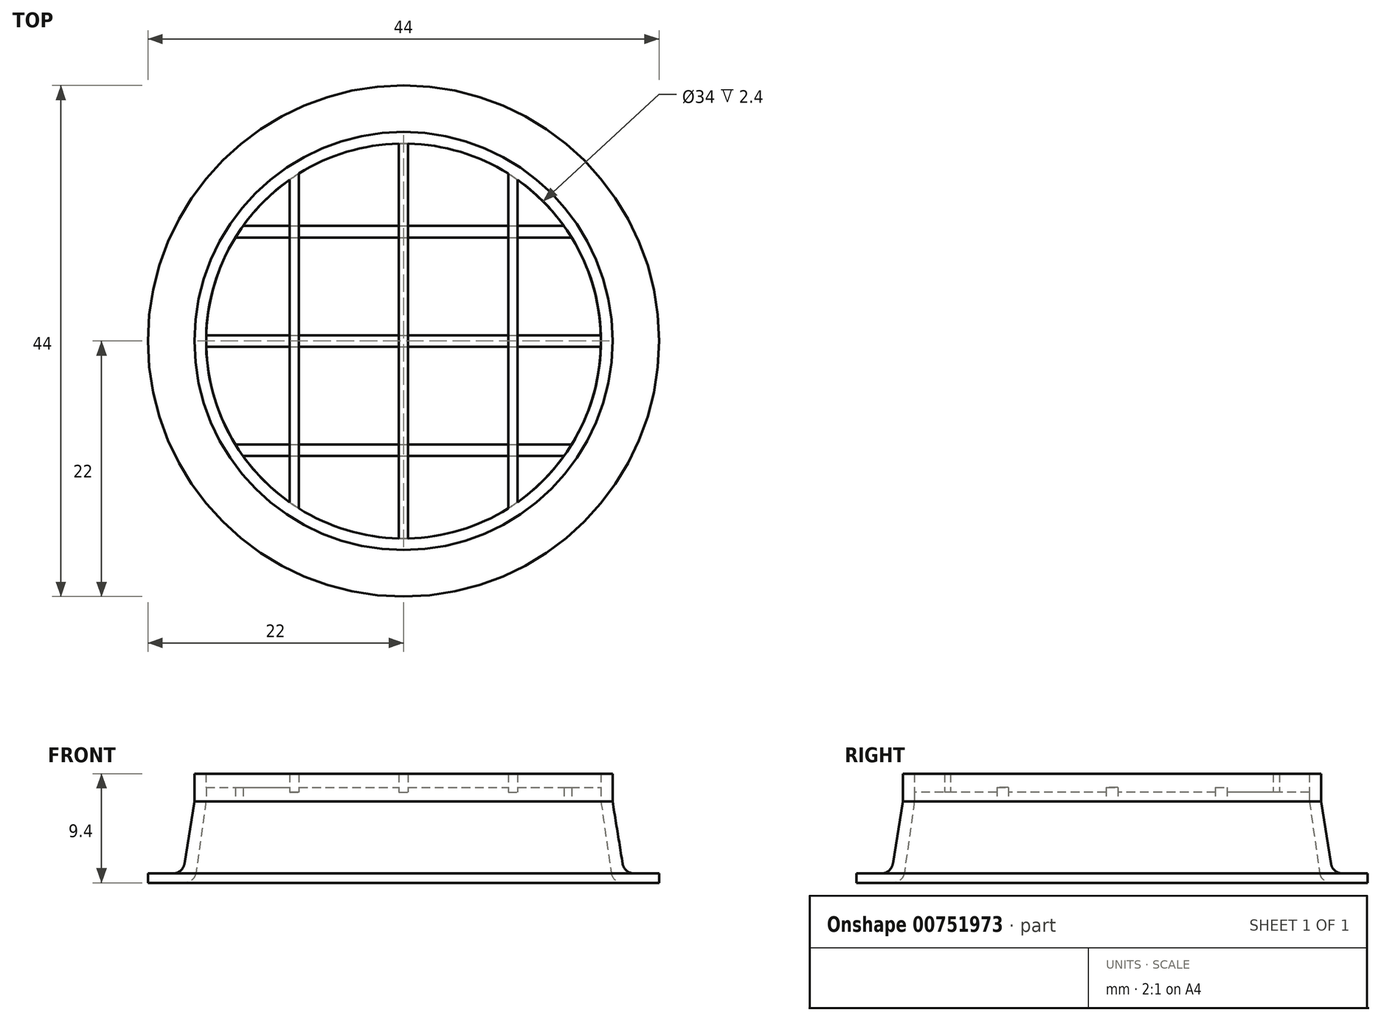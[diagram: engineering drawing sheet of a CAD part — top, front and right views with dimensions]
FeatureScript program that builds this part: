
annotation { "Feature Type Name" : "Feature", "Feature Type Description" : "" }
export const myFeature = defineFeature(function(context is Context, id is Id, definition is map)
    precondition{}
    {
        {
            var Q0;
            Q0=qCreatedBy(makeId("Front.planeOp"),FACE);
            var sketch = newSketch(context, id + "F0", { "sketchPlane" : qUnion([Q0])});
            skLineSegment(sketch, "E0", {"start": v(0, 16.66) * mm, "end": v(0, -15.75) * mm, "construction": true});
            skLineSegment(sketch, "E1", {"start": v(8.08, 0) * mm, "end": v(-29.3, 0) * mm, "construction": true});
            skLineSegment(sketch, "E2", {"start": v(1.58, 0) * mm, "end": v(-1.66, 0) * mm, "construction": true});
            skLineSegment(sketch, "E3", {"start": v(-1, 1.45) * mm, "end": v(-1, -7.95) * mm, "construction": true});
            skLineSegment(sketch, "E4", {"start": v(-5, -6.2) * mm, "end": v(-5, -8.06) * mm, "construction": true});
            skLineSegment(sketch, "E5", {"start": v(-5, -7) * mm, "end": v(-1.87, -7) * mm});
            skLineSegment(sketch, "E6", {"start": v(-0.88, -6.14) * mm, "end": v(0, 0) * mm});
            skLineSegment(sketch, "E7", {"start": v(0, 0) * mm, "end": v(-1, 0) * mm});
            skLineSegment(sketch, "E8", {"start": v(-1, 0) * mm, "end": v(-1.86, -5.36) * mm});
            skLineSegment(sketch, "E9", {"start": v(-2.85, -6.2) * mm, "end": v(-5, -6.2) * mm});
            skLineSegment(sketch, "E10", {"start": v(-5, -6.2) * mm, "end": v(-5, -7) * mm});
            skPoint(sketch, "E11.visualSharp", {"position": v(-2, -6.2) * mm});
            skArc(sketch, "E11.filletArc", {"start": v(-2.85, -6.2) * mm, "mid": v(-2.2, -5.96) * mm, "end": v(-1.86, -5.36) * mm});
            skPoint(sketch, "E12.visualSharp", {"position": v(-1, -7) * mm});
            skArc(sketch, "E12.filletArc", {"start": v(-1.87, -7) * mm, "mid": v(-1.21, -6.76) * mm, "end": v(-0.88, -6.14) * mm});
            skLineSegment(sketch, "E13", {"start": v(17, 0.36) * mm, "end": v(17, -7.36) * mm, "construction": true});
            skSolve(sketch);
        }
        {
            var Q0;
            Q0=qSketchRegion(id+"F0",true);
            var Q1;
            Q1=sQuery(id+"F0.wireOp",EDGE,"E13");
            revolve(context, id + "F1", {"surfaceOperationType" : NewSurfaceOperationType.NEW, "entities" : qUnion([Q0]), "axis" : qUnion([Q1]), "revolveType" : RevolveType.FULL});
        }
        {
            var Q0;
            Q0=makeQuery(id+"F1.opRevolve","SWEPT_FACE",FACE,{"disambiguationData":[OSD([sQuery(id+"F0.wireOp",EDGE,"E7")])]});
            var sketch = newSketch(context, id + "F2", { "sketchPlane" : qUnion([Q0])});
            skLineSegment(sketch, "E14", {"start": v(0, 0) * mm, "end": v(34, 0) * mm, "construction": true});
            skCircle(sketch, "E15.0", {"center": v(17, 0) * mm, "radius": 18 * mm});
            skLineSegment(sketch, "E16", {"start": v(-1, 0.5) * mm, "end": v(35, 0.5) * mm});
            skLineSegment(sketch, "E17.MirrorCS", {"start": v(-1, -0.5) * mm, "end": v(35, -0.5) * mm});
            skLineSegment(sketch, "E18", {"start": v(1.36, 8.91) * mm, "end": v(32.64, 8.91) * mm});
            skLineSegment(sketch, "E19", {"start": v(1.97, 9.91) * mm, "end": v(32.03, 9.91) * mm});
            skLineSegment(sketch, "E20.MirrorCS", {"start": v(1.36, -8.91) * mm, "end": v(32.64, -8.91) * mm});
            skLineSegment(sketch, "E21.MirrorCS", {"start": v(1.97, -9.91) * mm, "end": v(32.03, -9.91) * mm});
            skSolve(sketch);
        }
        {
            var Q0;
            {var subQ0=sQuery(id+"F2.wireOp",EDGE,"E18");var subQ1=makeQuery(id+"F1.opRevolve","SWEPT_EDGE",EDGE,{"disambiguationData":[OSD([sQuery(id+"F0.wireOp",EDGE,"E6"),sQuery(id+"F0.wireOp",EDGE,"E7")])]});var subQ2=makeQuery(id+"F2.imprint","INTERSECT",VERTEX,{"disambiguationData":[OD(0.0)],"derivedFrom":[subQ1,subQ0]});Q0=makeQuery(id+"F2.imprint","IMPRINT",FACE,{"disambiguationData":[TD([[makeQuery(id+"F2.imprint","IMPRINT",EDGE,{"disambiguationData":[TD([[subQ2,-1.0]])],"derivedFrom":subQ0}),1.0]])]});}
            var Q1;
            {var subQ0=sQuery(id+"F2.wireOp",EDGE,"E16");var subQ1=makeQuery(id+"F1.opRevolve","SWEPT_EDGE",EDGE,{"disambiguationData":[OSD([sQuery(id+"F0.wireOp",EDGE,"E6"),sQuery(id+"F0.wireOp",EDGE,"E7")])]});var subQ2=makeQuery(id+"F2.imprint","INTERSECT",VERTEX,{"disambiguationData":[OD(0.0)],"derivedFrom":[subQ1,subQ0]});Q1=makeQuery(id+"F2.imprint","IMPRINT",FACE,{"disambiguationData":[TD([[makeQuery(id+"F2.imprint","IMPRINT",EDGE,{"disambiguationData":[TD([[subQ2,-1.0]])],"derivedFrom":subQ0}),-1.0]])]});}
            var Q2;
            {var subQ0=sQuery(id+"F2.wireOp",EDGE,"E20.MirrorCS");var subQ1=makeQuery(id+"F1.opRevolve","SWEPT_EDGE",EDGE,{"disambiguationData":[OSD([sQuery(id+"F0.wireOp",EDGE,"E6"),sQuery(id+"F0.wireOp",EDGE,"E7")])]});var subQ2=makeQuery(id+"F2.imprint","INTERSECT",VERTEX,{"disambiguationData":[OD(0.0)],"derivedFrom":[subQ1,subQ0]});Q2=makeQuery(id+"F2.imprint","IMPRINT",FACE,{"disambiguationData":[TD([[makeQuery(id+"F2.imprint","IMPRINT",EDGE,{"disambiguationData":[TD([[subQ2,-1.0]])],"derivedFrom":subQ0}),-1.0]])]});}
            extrude(context, id + "F3", {"entities" : qUnion([Q0, Q1, Q2]), "depth" : 1.2 * mm, "offsetDistance" : 25 * mm});
        }
        {
            var Q0;
            Q0=makeQuery(id+"F1.opRevolve","SWEPT_FACE",FACE,{"disambiguationData":[OSD([sQuery(id+"F0.wireOp",EDGE,"E7")])]});
            var sketch = newSketch(context, id + "F4", { "sketchPlane" : qUnion([Q0])});
            skCircle(sketch, "E22.0", {"center": v(17, 0) * mm, "radius": 17 * mm});
            skCircle(sketch, "E23.0", {"center": v(17, 0) * mm, "radius": 18 * mm});
            skSolve(sketch);
        }
        {
            var Q0;
            Q0=qSketchRegion(id+"F4",true);
            extrude(context, id + "F5", {"entities" : qUnion([Q0]), "depth" : 1.2 * mm, "offsetDistance" : 25 * mm});
        }
        {
            var Q0;
            Q0=makeQuery(id+"F5.opExtrude","CAP_FACE",FACE,{"disambiguationData":[OSD([sQuery(id+"F4.wireOp",EDGE,"E22.0"),sQuery(id+"F4.wireOp",EDGE,"E23.0")])],"isStart":false});
            var sketch = newSketch(context, id + "F6", { "sketchPlane" : qUnion([Q0])});
            skLineSegment(sketch, "E24", {"start": v(17, 17) * mm, "end": v(17, -17) * mm, "construction": true});
            skLineSegment(sketch, "E25", {"start": v(17.4, 17) * mm, "end": v(17.4, -17) * mm});
            skLineSegment(sketch, "E26", {"start": v(26.01, 14.41) * mm, "end": v(26.01, -14.41) * mm});
            skLineSegment(sketch, "E27", {"start": v(26.81, 13.88) * mm, "end": v(26.81, -13.88) * mm});
            skLineSegment(sketch, "E28.MirrorCS", {"start": v(16.6, 17) * mm, "end": v(16.6, -17) * mm});
            skLineSegment(sketch, "E29.MirrorCS", {"start": v(7.99, 14.41) * mm, "end": v(7.99, -14.41) * mm});
            skLineSegment(sketch, "E30.MirrorCS", {"start": v(7.19, 13.88) * mm, "end": v(7.19, -13.88) * mm});
            skCircle(sketch, "E31.0", {"center": v(17, 0) * mm, "radius": 18 * mm});
            skCircle(sketch, "E32.0", {"center": v(17, 0) * mm, "radius": 17 * mm});
            skLineSegment(sketch, "E33", {"start": v(7.19, 13.88) * mm, "end": v(7.99, 14.41) * mm});
            skLineSegment(sketch, "E34", {"start": v(16.6, 17) * mm, "end": v(17.4, 17) * mm});
            skLineSegment(sketch, "E35", {"start": v(26.01, 14.41) * mm, "end": v(26.81, 13.88) * mm});
            skLineSegment(sketch, "E36", {"start": v(26.81, -13.88) * mm, "end": v(26.01, -14.41) * mm});
            skLineSegment(sketch, "E37", {"start": v(17.4, -17) * mm, "end": v(16.6, -17) * mm});
            skLineSegment(sketch, "E38", {"start": v(7.99, -14.41) * mm, "end": v(7.19, -13.88) * mm});
            skSolve(sketch);
        }
        {
            var Q0;
            Q0=qSketchRegion(id+"F6",true);
            var Q1;
            Q1=makeQuery(id+"F6.imprint","IMPRINT",FACE,{"disambiguationData":[TD([[makeQuery(id+"F6.imprint","IMPRINT",EDGE,{"derivedFrom":sQuery(id+"F6.wireOp",EDGE,"E29.MirrorCS")}),-1.0]])]});
            var Q2;
            Q2=makeQuery(id+"F6.imprint","IMPRINT",FACE,{"disambiguationData":[TD([[makeQuery(id+"F6.imprint","IMPRINT",EDGE,{"derivedFrom":sQuery(id+"F6.wireOp",EDGE,"E25")}),-1.0]])]});
            var Q3;
            Q3=makeQuery(id+"F6.imprint","IMPRINT",FACE,{"disambiguationData":[TD([[makeQuery(id+"F6.imprint","IMPRINT",EDGE,{"derivedFrom":sQuery(id+"F6.wireOp",EDGE,"E26")}),1.0]])]});
            extrude(context, id + "F7", {"entities" : qUnion([Q0, Q1, Q2, Q3]), "operationType" : NewBodyOperationType.ADD, "depth" : 1.2 * mm, "offsetDistance" : 25 * mm, "hasSecondDirection" : true, "secondDirectionOppositeDirection" : true, "secondDirectionDepth" : .4 * mm});
        }
    });
